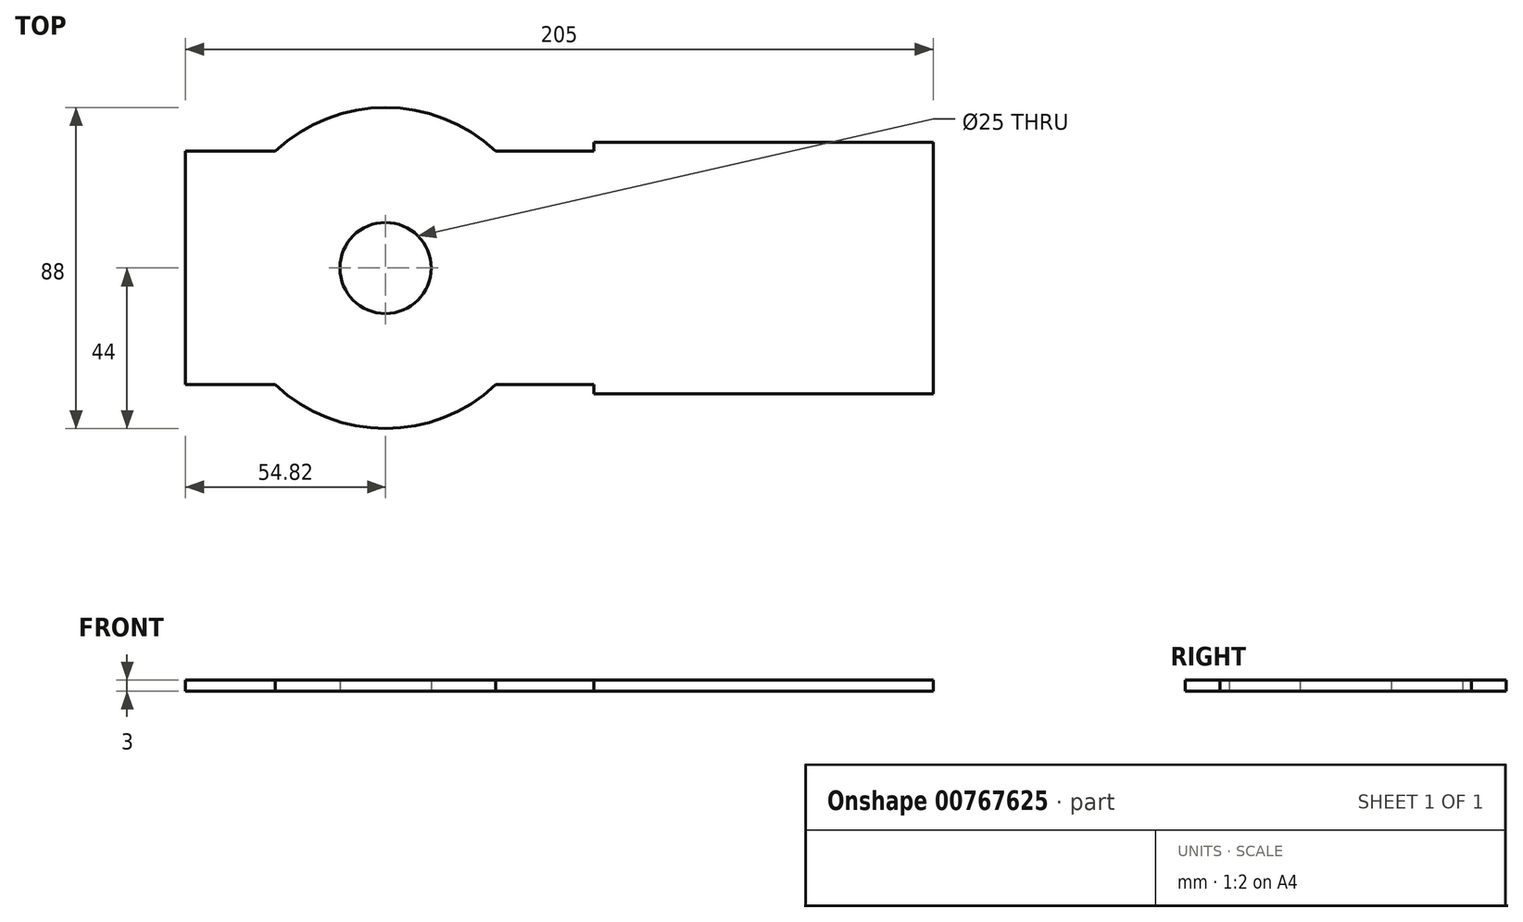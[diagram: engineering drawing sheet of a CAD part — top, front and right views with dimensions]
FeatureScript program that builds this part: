
annotation { "Feature Type Name" : "Feature", "Feature Type Description" : "" }
export const myFeature = defineFeature(function(context is Context, id is Id, definition is map)
    precondition{}
    {
        {
            var Q0;
            Q0=qCreatedBy(makeId("Top.planeOp"),FACE);
            var sketch = newSketch(context, id + "F0", { "sketchPlane" : qUnion([Q0])});
            skArc(sketch, "E0", {"start": v(12.5, 0) * mm, "mid": v(0, 12.5) * mm, "end": v(-12.5, 0) * mm});
            skLineSegment(sketch, "E1.bottom", {"start": v(-30.02, 32) * mm, "end": v(-54.82, 32) * mm});
            skLineSegment(sketch, "E1.right", {"start": v(-54.82, 32) * mm, "end": v(-54.82, 0) * mm});
            skArc(sketch, "E2", {"start": v(30.2, 32) * mm, "mid": v(0, 44) * mm, "end": v(-30.2, 32) * mm});
            skLineSegment(sketch, "E3", {"start": v(57.18, 34.46) * mm, "end": v(150.18, 34.46) * mm});
            skLineSegment(sketch, "E4", {"start": v(30.2, 32) * mm, "end": v(57.18, 32) * mm});
            skLineSegment(sketch, "E5.trimOffspring", {"start": v(57.18, 32) * mm, "end": v(57.18, 34.46) * mm});
            skLineSegment(sketch, "E6", {"start": v(150.18, 34.46) * mm, "end": v(150.18, 0) * mm});
            skLineSegment(sketch, "E7.MirrorCS", {"start": v(57.18, -32) * mm, "end": v(57.18, -34.46) * mm});
            skLineSegment(sketch, "E8.MirrorCS", {"start": v(30.2, -32) * mm, "end": v(57.18, -32) * mm});
            skLineSegment(sketch, "E9.MirrorCS", {"start": v(-30.02, -32) * mm, "end": v(-54.82, -32) * mm});
            skLineSegment(sketch, "E10.MirrorCS", {"start": v(57.18, -34.46) * mm, "end": v(150.18, -34.46) * mm});
            skLineSegment(sketch, "E11.MirrorCS", {"start": v(-54.82, -32) * mm, "end": v(-54.82, 0) * mm});
            skLineSegment(sketch, "E12.MirrorCS", {"start": v(150.18, -34.46) * mm, "end": v(150.18, 0) * mm});
            skArc(sketch, "E13.MirrorCS", {"start": v(12.5, 0) * mm, "mid": v(0, -12.5) * mm, "end": v(-12.5, 0) * mm});
            skArc(sketch, "E14.MirrorCS", {"start": v(30.2, -32) * mm, "mid": v(0, -44) * mm, "end": v(-30.2, -32) * mm});
            skSolve(sketch);
        }
        {
            var Q0;
            Q0=makeQuery(id+"F0.imprint","IMPRINT",FACE,{"disambiguationData":[TD([[makeQuery(id+"F0.imprint","IMPRINT",EDGE,{"derivedFrom":sQuery(id+"F0.wireOp",EDGE,"E0")}),-1.0]])]});
            extrude(context, id + "F1", {"entities" : qUnion([Q0]), "depth" : 3 * mm, "offsetDistance" : 25 * mm});
        }
    });
